# Revit family: РОСМА_МанометрПовышКлассТочн
name_source: partatom
category: Арматура трубопроводов
revit_build: Autodesk Revit 2018 (Build: 20180423_1000(x64)
units: mm (PartAtom-declared; Revit-internal decimal feet)

## family parameters
Всегда вертикально = Да
На основе рабочей плоскости = Нет
Общий = Нет
При загрузке вырезать с полостями = Нет
Размер круглого соединителя = Использовать диаметр
Тип детали = Вставляется

## types (3) — shared parameters
ADSK_Единица измерения = шт.
ADSK_Количество = 1
Table = спец_повышенный к.т.
Table_2 = размеры_повышенный к.т.
URL = https://rosma.spb.ru
Группа модели = Оборудование
Давление01 = ‎ : ТВ -0,1…0МПа
Давление03 = ‎ : ТМ 0…0,1МПа
Давление04 = ‎ : ТМ 0…0,16МПа
Давление05 = ‎ : ТМ 0…0,25МПа
Давление06 = ‎ : ТМ 0…0,4МПа
Давление07 = ‎ : ТМ 0…0,6МПа
Давление08 = ‎ : ТМ 0…1,0МПа
Давление09 = ‎ : ТМ 0…1,6МПа
Давление10 = ‎ : ТМ 0…2,5МПа
Давление11 = ‎ : ТМ 0…4МПа
Давление12 = ‎ : ТМ 0…6МПа
Давление13 = ‎ : ТМ 0…10МПа
Давление14 = ‎ : ТМ 0…16МПа
Давление15 = ‎ : ТМ 0…25МПа
Давление16 = ‎ : ТМ 0…40МПа
Давление17 = ‎ : ТМ 0…60МПа
Давление18 = ‎ : ТМ 0…100МПа
Давление19 = ‎ : ТМВ -0,1…0,15МПа
Давление20 = ‎ : ТМВ -0,1…0,3МПа
Давление21 = ‎ : ТМВ -0,1…0,5МПа
Давление22 = ‎ : ТМВ -0,1…0,9МПа
Давление23 = ‎ : ТМВ -0,1…1,5МПа
Давление24 = ‎ : ТМВ -0,1…2,4МПа
Изготовитель = ЗАО "РОСМА"
Климатическое исполнение = Группа В3 по ГОСТ Р 52931; климатическое исполнение УХЛ категории 3.1 по ГОСТ 15150
Код IP = IP40
Межповерочный интервал = 2 года
Описание = Манометр показывающий ТМ серия 10, с повышенным классом точности.
Техническая документация = ТУ 4212-001-4719015564-2008; ГОСТ 2405–88
лого_задн_стенка = Да

## per-type parameters (varying)
| type | Ddempfer | Класс точности |
| 310 | 5 мм | 1,5 |
| 510 | 6 мм | 1,0 |
| 610 | 6 мм | 1,0 |

note: column(s) folded — value = type name in every type: Исполнение
